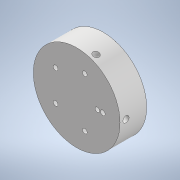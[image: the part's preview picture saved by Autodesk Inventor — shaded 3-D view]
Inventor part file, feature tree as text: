
AUTODESK INVENTOR PART (.ipt)
format: ipt  version: 2022 (Build 260153000, 153)  size: 327,680 bytes
history: native  units: mm
features: other x6, sketch x5, extrude x4, pattern_circular x3, reference x3, plane x1, sweep x1
ambient origin geometry x8: Origin, YZ Plane, XZ Plane, XY Plane, X Axis, Y Axis, Z Axis, Center Point
bodies: Solid1 (feature_tree)
feature tree (23):
  extrude  "Extrusion1"  Depth=38.798324mm
  plane  "Work Plane1"
  extrude  "Extrusion2"  Depth=50.0mm TaperAngle=360.0deg
  pattern_circular  "Circular Pattern1"  Count=5 Angle=360.0deg
  extrude  "Extrusion3"  Depth=3.5mm TaperAngle=0.0deg
  sweep  "Sweep1"
  pattern_circular  "Circular Pattern2"  [2 undecoded]
  extrude  "Extrusion4"  TaperAngle=0.0deg  [1 undecoded]
  pattern_circular  "Circular Pattern3"  Count=5 Angle=360.0deg
  sketch  "Sketch1"  dims[d0=28.798324mm d1=38.798324mm]
  reference  "Reference1"
  sketch  "Sketch2"  dims[d2=20.0mm d3=50.0mm d5=360.0deg]
  reference  "Reference2"
  reference  "Reference3"
  sketch  "Sketch4"  dims[d7=1.0mm d8=9.0mm d9=0.0mm d10=0.0mm]
  sketch  "Sketch5"  dims[d11=1.0mm d12=0.0mm d13=50.0mm d14=360.0deg]
  sketch  "Sketch6"  dims[d16=50.0mm d18=360.0deg d20=20.0mm d21=0.0mm d22=7.0mm d23=3.5mm d24=0.0mm d25=0.0mm d26=50.0mm d27=360.0deg d29=5.0mm d30=0.0mm d31=0.0mm d32=50.0mm d33=360.0deg]
  other  "<userpath>\OneDrive - Imperial College London\ROBOICP\new vial holder assembly.iam"
  other  "new vial holder assembly.iam"
  other  "vial thread insert:1"
  other  "vial:1"
  other  "mixer_gear:1"
  other  "Assembly1"
note: 3 required parameter values undecoded (feature->parameter linkage not recoverable at this tier; creation-order binding heuristic only, values carry confidence <= 0.55)
